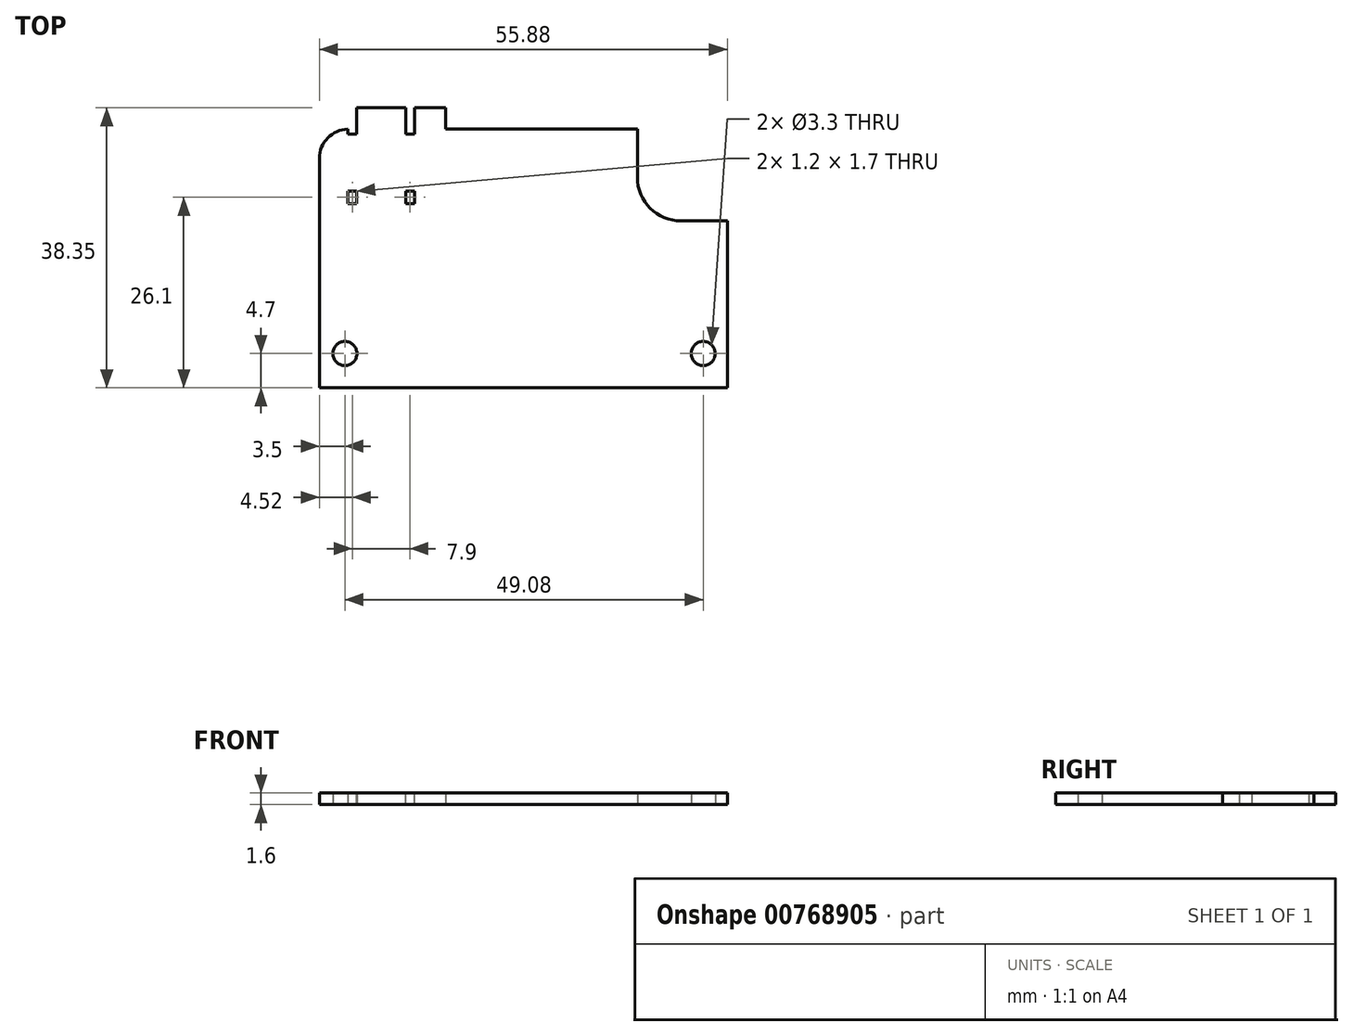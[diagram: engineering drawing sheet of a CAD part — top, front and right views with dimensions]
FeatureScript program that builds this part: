
annotation { "Feature Type Name" : "Feature", "Feature Type Description" : "" }
export const myFeature = defineFeature(function(context is Context, id is Id, definition is map)
    precondition{}
    {
        {
            var Q0;
            Q0=qCreatedBy(makeId("Top.planeOp"),FACE);
            var sketch = newSketch(context, id + "F0", { "sketchPlane" : qUnion([Q0])});
            skLineSegment(sketch, "E0", {"start": v(0, 0) * mm, "end": v(0, 35.43) * mm});
            skLineSegment(sketch, "E1", {"start": v(0, 35.43) * mm, "end": v(4.57, 35.43) * mm});
            skLineSegment(sketch, "E2", {"start": v(4.57, 35.43) * mm, "end": v(4.57, 38.35) * mm});
            skLineSegment(sketch, "E3", {"start": v(4.57, 38.35) * mm, "end": v(17.27, 38.35) * mm});
            skLineSegment(sketch, "E4", {"start": v(17.27, 38.35) * mm, "end": v(17.27, 35.43) * mm});
            skLineSegment(sketch, "E5", {"start": v(17.27, 35.43) * mm, "end": v(43.56, 35.43) * mm});
            skCircle(sketch, "E6", {"center": v(3.5, 4.7) * mm, "radius": 1.65 * mm});
            skLineSegment(sketch, "E7", {"start": v(43.56, 35.43) * mm, "end": v(43.56, 22.86) * mm});
            skLineSegment(sketch, "E8", {"start": v(43.56, 22.86) * mm, "end": v(55.88, 22.86) * mm});
            skLineSegment(sketch, "E9", {"start": v(55.88, 22.86) * mm, "end": v(55.88, 0) * mm});
            skLineSegment(sketch, "E10", {"start": v(55.88, 0) * mm, "end": v(0, 0) * mm});
            skCircle(sketch, "E11", {"center": v(52.58, 4.7) * mm, "radius": 1.65 * mm});
            skLineSegment(sketch, "E12", {"start": v(4.57, 35.43) * mm, "end": v(17.27, 35.43) * mm, "construction": true});
            skLineSegment(sketch, "E13", {"start": v(3.5, 4.7) * mm, "end": v(52.58, 4.7) * mm, "construction": true});
            skSolve(sketch);
        }
        {
            var Q0;
            Q0 = qSketchRegion(id + "F0", true);
            extrude(context, id + "F1", {"entities" : qUnion([Q0]), "depth" : 1.6 * mm, "offsetDistance" : 25 * mm});
        }
        {
            var Q0;
            Q0=makeQuery(id+"F1.opExtrude","SWEPT_EDGE",EDGE,{"disambiguationData":[OSD([sQuery(id+"F0.wireOp",EDGE,"E0"),sQuery(id+"F0.wireOp",EDGE,"E1")])]});
            fillet(context, id + "F2", {"entities" : qUnion([Q0]), "radius" : 4 * mm, "tangentPropagation" : true, "allowEdgeOverflow" : false});
        }
        {
            var Q0;
            Q0=makeQuery(id+"F1.opExtrude","SWEPT_EDGE",EDGE,{"disambiguationData":[OSD([sQuery(id+"F0.wireOp",EDGE,"E7"),sQuery(id+"F0.wireOp",EDGE,"E8")])]});
            fillet(context, id + "F3", {"entities" : qUnion([Q0]), "radius" : 6 * mm, "tangentPropagation" : true, "allowEdgeOverflow" : false});
        }
        {
            var Q0;
            Q0=makeQuery(id+"F1.opExtrude","CAP_FACE",FACE,{"disambiguationData":[OSD([sQuery(id+"F0.wireOp",EDGE,"E0"),sQuery(id+"F0.wireOp",EDGE,"E1"),sQuery(id+"F0.wireOp",EDGE,"E2"),sQuery(id+"F0.wireOp",EDGE,"E3"),sQuery(id+"F0.wireOp",EDGE,"E4"),sQuery(id+"F0.wireOp",EDGE,"E5"),sQuery(id+"F0.wireOp",EDGE,"E6"),sQuery(id+"F0.wireOp",EDGE,"E7"),sQuery(id+"F0.wireOp",EDGE,"E8"),sQuery(id+"F0.wireOp",EDGE,"E9"),sQuery(id+"F0.wireOp",EDGE,"E10"),sQuery(id+"F0.wireOp",EDGE,"E11")])],"isStart":false});
            var sketch = newSketch(context, id + "F4", { "sketchPlane" : qUnion([Q0])});
            skLineSegment(sketch, "E14.bottom", {"start": v(5.12, 38.35) * mm, "end": v(3.92, 38.35) * mm});
            skLineSegment(sketch, "E14.top", {"start": v(5.12, 34.75) * mm, "end": v(3.92, 34.75) * mm});
            skLineSegment(sketch, "E14.left", {"start": v(5.12, 38.35) * mm, "end": v(5.12, 34.75) * mm});
            skLineSegment(sketch, "E14.right", {"start": v(3.92, 38.35) * mm, "end": v(3.92, 34.75) * mm});
            skLineSegment(sketch, "E15.bottom", {"start": v(11.82, 38.35) * mm, "end": v(13.02, 38.35) * mm});
            skLineSegment(sketch, "E15.top", {"start": v(11.82, 34.75) * mm, "end": v(13.02, 34.75) * mm});
            skLineSegment(sketch, "E15.left", {"start": v(11.82, 38.35) * mm, "end": v(11.82, 34.75) * mm});
            skLineSegment(sketch, "E15.right", {"start": v(13.02, 38.35) * mm, "end": v(13.02, 34.75) * mm});
            skLineSegment(sketch, "E16.bottom", {"start": v(3.92, 26.95) * mm, "end": v(5.12, 26.95) * mm});
            skLineSegment(sketch, "E16.top", {"start": v(3.92, 25.25) * mm, "end": v(5.12, 25.25) * mm});
            skLineSegment(sketch, "E16.left", {"start": v(3.92, 26.95) * mm, "end": v(3.92, 25.25) * mm});
            skLineSegment(sketch, "E16.right", {"start": v(5.12, 26.95) * mm, "end": v(5.12, 25.25) * mm});
            skLineSegment(sketch, "E17.bottom", {"start": v(11.82, 26.95) * mm, "end": v(13.02, 26.95) * mm});
            skLineSegment(sketch, "E17.top", {"start": v(11.82, 25.25) * mm, "end": v(13.02, 25.25) * mm});
            skLineSegment(sketch, "E17.left", {"start": v(11.82, 26.95) * mm, "end": v(11.82, 25.25) * mm});
            skLineSegment(sketch, "E17.right", {"start": v(13.02, 26.95) * mm, "end": v(13.02, 25.25) * mm});
            skLineSegment(sketch, "E18", {"start": v(3.92, 26.95) * mm, "end": v(3.92, 34.75) * mm, "construction": true});
            skLineSegment(sketch, "E19", {"start": v(5.12, 26.95) * mm, "end": v(5.12, 34.75) * mm, "construction": true});
            skLineSegment(sketch, "E20", {"start": v(11.82, 26.95) * mm, "end": v(11.82, 34.75) * mm, "construction": true});
            skLineSegment(sketch, "E21", {"start": v(13.02, 26.95) * mm, "end": v(13.02, 34.75) * mm, "construction": true});
            skSolve(sketch);
        }
        {
            var Q0;
            Q0 = qSketchRegion(id + "F4", true);
            extrude(context, id + "F5", {"entities" : qUnion([Q0]), "operationType" : NewBodyOperationType.REMOVE, "endBound" : BoundingType.THROUGH_ALL, "oppositeDirection" : true, "depth" : 25 * mm, "offsetDistance" : 25 * mm});
        }
    });
